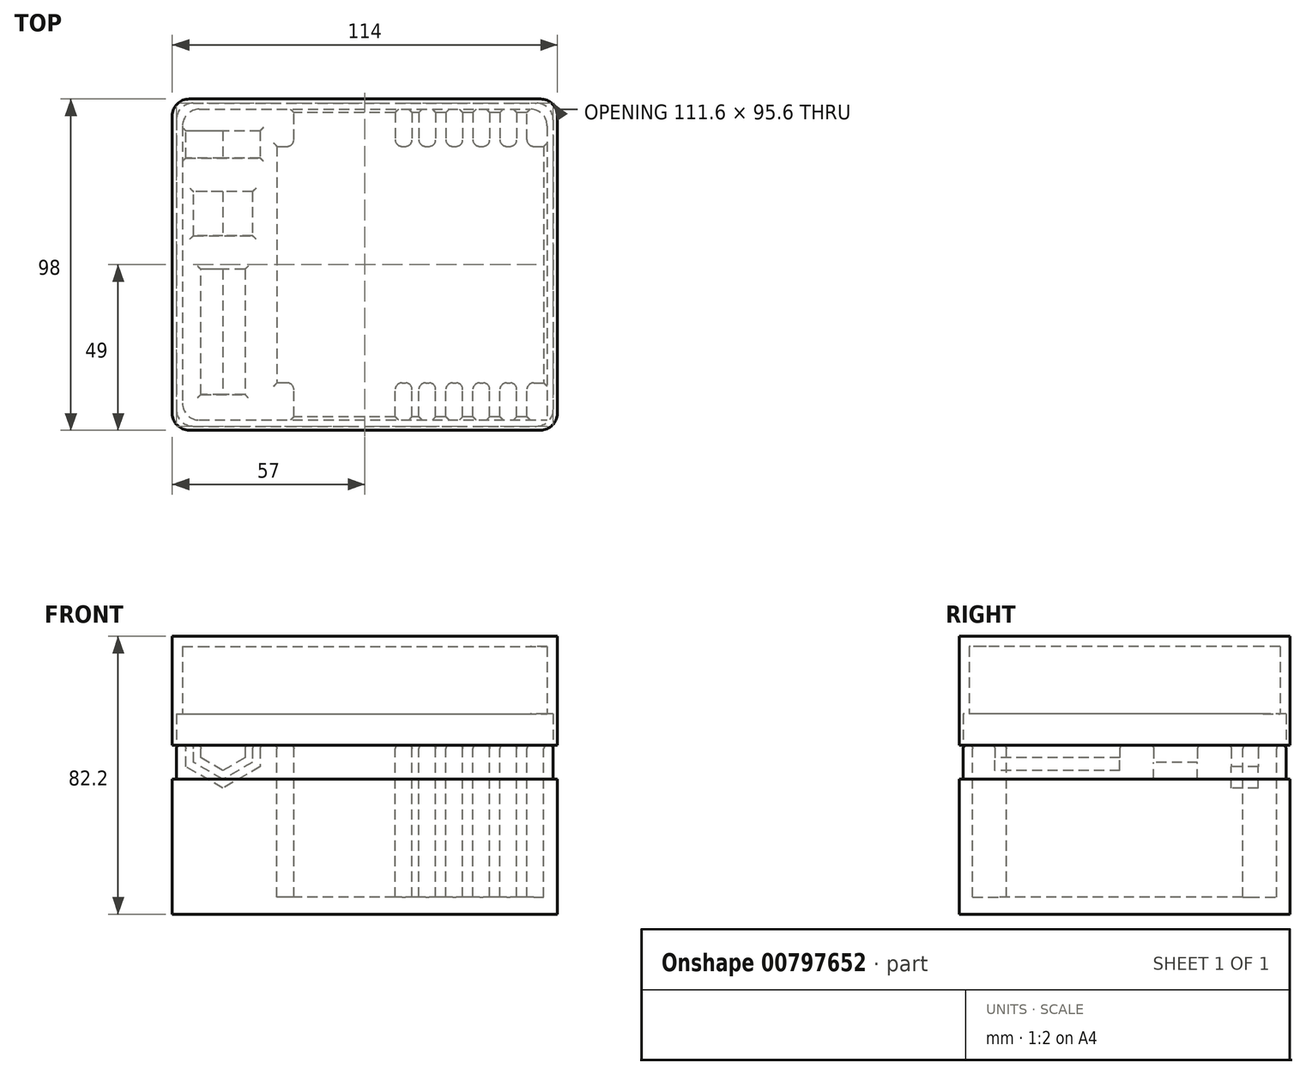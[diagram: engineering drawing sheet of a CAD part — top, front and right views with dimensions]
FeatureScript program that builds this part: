
annotation { "Feature Type Name" : "Feature", "Feature Type Description" : "" }
export const myFeature = defineFeature(function(context is Context, id is Id, definition is map)
    precondition{}
    {
        {
            var Q0;
            Q0=qCreatedBy(makeId("Top.planeOp"),FACE);
            var sketch = newSketch(context, id + "F0", { "sketchPlane" : qUnion([Q0])});
            skLineSegment(sketch, "E0.bottom", {"start": v(34.5, -45) * mm, "end": v(31.5, -45) * mm});
            skLineSegment(sketch, "E0.top", {"start": v(34.5, 45) * mm, "end": v(31.5, 45) * mm});
            skLineSegment(sketch, "E0.left", {"start": v(34.5, -45) * mm, "end": v(34.5, -35) * mm});
            skLineSegment(sketch, "E0.right", {"start": v(-34.5, -45) * mm, "end": v(-34.5, -35) * mm});
            skPoint(sketch, "E0.middle", {"position": v(0, 0) * mm});
            skLineSegment(sketch, "E1.top", {"start": v(-4.5, 35) * mm, "end": v(0.5, 35) * mm});
            skLineSegment(sketch, "E1.left", {"start": v(-4.5, 45) * mm, "end": v(-4.5, 35) * mm});
            skLineSegment(sketch, "E1.right", {"start": v(0.5, 45) * mm, "end": v(0.5, 35) * mm});
            skLineSegment(sketch, "E2.top", {"start": v(2.5, 35) * mm, "end": v(7.5, 35) * mm});
            skLineSegment(sketch, "E2.left", {"start": v(2.5, 45) * mm, "end": v(2.5, 35) * mm});
            skLineSegment(sketch, "E2.right", {"start": v(7.5, 45) * mm, "end": v(7.5, 35) * mm});
            skLineSegment(sketch, "E3.top", {"start": v(10.5, 35) * mm, "end": v(15.5, 35) * mm});
            skLineSegment(sketch, "E3.left", {"start": v(10.5, 45) * mm, "end": v(10.5, 35) * mm});
            skLineSegment(sketch, "E3.right", {"start": v(15.5, 45) * mm, "end": v(15.5, 35) * mm});
            skLineSegment(sketch, "E4.top", {"start": v(18.5, 35) * mm, "end": v(23.5, 35) * mm});
            skLineSegment(sketch, "E4.left", {"start": v(18.5, 45) * mm, "end": v(18.5, 35) * mm});
            skLineSegment(sketch, "E4.right", {"start": v(23.5, 45) * mm, "end": v(23.5, 35) * mm});
            skLineSegment(sketch, "E5.top", {"start": v(26.5, 35) * mm, "end": v(31.5, 35) * mm});
            skLineSegment(sketch, "E5.left", {"start": v(26.5, 45) * mm, "end": v(26.5, 35) * mm});
            skLineSegment(sketch, "E5.right", {"start": v(31.5, 45) * mm, "end": v(31.5, 35) * mm});
            skLineSegment(sketch, "E6.trimOffspring", {"start": v(-4.5, 45) * mm, "end": v(-34.5, 45) * mm});
            skLineSegment(sketch, "E7.trimOffspring", {"start": v(2.5, 45) * mm, "end": v(0.5, 45) * mm});
            skLineSegment(sketch, "E8.trimOffspring", {"start": v(10.5, 45) * mm, "end": v(7.5, 45) * mm});
            skLineSegment(sketch, "E9.trimOffspring", {"start": v(18.5, 45) * mm, "end": v(15.5, 45) * mm});
            skLineSegment(sketch, "E10.trimOffspring", {"start": v(26.5, 45) * mm, "end": v(23.5, 45) * mm});
            skLineSegment(sketch, "E11.MirrorCS", {"start": v(-4.5, -45) * mm, "end": v(-4.5, -35) * mm});
            skLineSegment(sketch, "E12.MirrorCS", {"start": v(0.5, -45) * mm, "end": v(0.5, -35) * mm});
            skLineSegment(sketch, "E13.MirrorCS", {"start": v(2.5, -45) * mm, "end": v(0.5, -45) * mm});
            skLineSegment(sketch, "E14.MirrorCS", {"start": v(2.5, -45) * mm, "end": v(2.5, -35) * mm});
            skLineSegment(sketch, "E15.MirrorCS", {"start": v(7.5, -45) * mm, "end": v(7.5, -35) * mm});
            skLineSegment(sketch, "E16.MirrorCS", {"start": v(10.5, -45) * mm, "end": v(7.5, -45) * mm});
            skLineSegment(sketch, "E17.MirrorCS", {"start": v(10.5, -45) * mm, "end": v(10.5, -35) * mm});
            skLineSegment(sketch, "E18.MirrorCS", {"start": v(15.5, -45) * mm, "end": v(15.5, -35) * mm});
            skLineSegment(sketch, "E19.MirrorCS", {"start": v(18.5, -45) * mm, "end": v(18.5, -35) * mm});
            skLineSegment(sketch, "E20.MirrorCS", {"start": v(18.5, -45) * mm, "end": v(15.5, -45) * mm});
            skLineSegment(sketch, "E21.MirrorCS", {"start": v(26.5, -45) * mm, "end": v(23.5, -45) * mm});
            skLineSegment(sketch, "E22.MirrorCS", {"start": v(23.5, -45) * mm, "end": v(23.5, -35) * mm});
            skLineSegment(sketch, "E23.MirrorCS", {"start": v(26.5, -45) * mm, "end": v(26.5, -35) * mm});
            skLineSegment(sketch, "E24.MirrorCS", {"start": v(31.5, -45) * mm, "end": v(31.5, -35) * mm});
            skLineSegment(sketch, "E25.MirrorCS", {"start": v(-4.5, -35) * mm, "end": v(0.5, -35) * mm});
            skLineSegment(sketch, "E26.MirrorCS", {"start": v(2.5, -35) * mm, "end": v(7.5, -35) * mm});
            skLineSegment(sketch, "E27.MirrorCS", {"start": v(10.5, -35) * mm, "end": v(15.5, -35) * mm});
            skLineSegment(sketch, "E28.MirrorCS", {"start": v(18.5, -35) * mm, "end": v(23.5, -35) * mm});
            skLineSegment(sketch, "E29.MirrorCS", {"start": v(26.5, -35) * mm, "end": v(31.5, -35) * mm});
            skLineSegment(sketch, "E30", {"start": v(-39.5, 35) * mm, "end": v(-39.5, -35) * mm});
            skLineSegment(sketch, "E31", {"start": v(-39.5, 35) * mm, "end": v(-34.5, 35) * mm});
            skLineSegment(sketch, "E32", {"start": v(-34.5, -35) * mm, "end": v(-39.5, -35) * mm});
            skLineSegment(sketch, "E33", {"start": v(39.5, 35) * mm, "end": v(39.5, -35) * mm});
            skLineSegment(sketch, "E34", {"start": v(34.5, 35) * mm, "end": v(39.5, 35) * mm});
            skLineSegment(sketch, "E35.trimOffspring", {"start": v(-34.5, 35) * mm, "end": v(-34.5, 45) * mm});
            skLineSegment(sketch, "E36.trimOffspring", {"start": v(34.5, 35) * mm, "end": v(34.5, 45) * mm});
            skLineSegment(sketch, "E37", {"start": v(34.5, -35) * mm, "end": v(39.5, -35) * mm});
            skPoint(sketch, "E38.orphan", {"position": v(-39.5, -45) * mm});
            skLineSegment(sketch, "E39.trimOffspring", {"start": v(-4.5, -45) * mm, "end": v(-34.5, -45) * mm});
            skLineSegment(sketch, "E40", {"start": v(-55.5, 78.4) * mm, "end": v(-55.5, -67.4) * mm, "construction": true});
            skLineSegment(sketch, "E41.bottom", {"start": v(-44.5, 31.59) * mm, "end": v(-66.5, 31.59) * mm});
            skLineSegment(sketch, "E41.top", {"start": v(-44.5, 39.59) * mm, "end": v(-66.5, 39.59) * mm});
            skLineSegment(sketch, "E41.left", {"start": v(-44.5, 31.59) * mm, "end": v(-44.5, 39.59) * mm});
            skLineSegment(sketch, "E41.right", {"start": v(-66.5, 31.59) * mm, "end": v(-66.5, 39.59) * mm});
            skPoint(sketch, "E41.middle", {"position": v(-55.5, 35.59) * mm});
            skLineSegment(sketch, "E42.bottom", {"start": v(-46.75, 8.59) * mm, "end": v(-64.25, 8.59) * mm});
            skLineSegment(sketch, "E42.top", {"start": v(-46.75, 21.59) * mm, "end": v(-64.25, 21.59) * mm});
            skLineSegment(sketch, "E42.left", {"start": v(-46.75, 8.59) * mm, "end": v(-46.75, 21.59) * mm});
            skLineSegment(sketch, "E42.right", {"start": v(-64.25, 8.59) * mm, "end": v(-64.25, 21.59) * mm});
            skPoint(sketch, "E42.middle", {"position": v(-55.5, 15.09) * mm});
            skLineSegment(sketch, "E43.bottom", {"start": v(-49, -38.41) * mm, "end": v(-62, -38.41) * mm});
            skLineSegment(sketch, "E43.top", {"start": v(-49, -1.41) * mm, "end": v(-62, -1.41) * mm});
            skLineSegment(sketch, "E43.left", {"start": v(-49, -38.41) * mm, "end": v(-49, -1.41) * mm});
            skLineSegment(sketch, "E43.right", {"start": v(-62, -38.41) * mm, "end": v(-62, -1.41) * mm});
            skPoint(sketch, "E43.middle", {"position": v(-55.5, -19.91) * mm});
            skLineSegment(sketch, "E44.bottom", {"start": v(-70.5, 49) * mm, "end": v(43.5, 49) * mm});
            skLineSegment(sketch, "E44.top", {"start": v(-70.5, -49) * mm, "end": v(43.5, -49) * mm});
            skLineSegment(sketch, "E44.left", {"start": v(-70.5, 49) * mm, "end": v(-70.5, -49) * mm});
            skLineSegment(sketch, "E44.right", {"start": v(43.5, 49) * mm, "end": v(43.5, -49) * mm});
            skSolve(sketch);
        }
        {
            var Q0;
            Q0=makeQuery(id+"F0.imprint","IMPRINT",FACE,{"disambiguationData":[TD([[makeQuery(id+"F0.imprint","IMPRINT",EDGE,{"derivedFrom":sQuery(id+"F0.wireOp",EDGE,"E0.top")}),-1.0]])]});
            var Q1;
            Q1=makeQuery(id+"F0.imprint","IMPRINT",FACE,{"disambiguationData":[TD([[makeQuery(id+"F0.imprint","IMPRINT",EDGE,{"derivedFrom":sQuery(id+"F0.wireOp",EDGE,"E41.bottom")}),-1.0]])]});
            var Q2;
            Q2=makeQuery(id+"F0.imprint","IMPRINT",FACE,{"disambiguationData":[TD([[makeQuery(id+"F0.imprint","IMPRINT",EDGE,{"derivedFrom":sQuery(id+"F0.wireOp",EDGE,"E42.bottom")}),-1.0]])]});
            var Q3;
            Q3=makeQuery(id+"F0.imprint","IMPRINT",FACE,{"disambiguationData":[TD([[makeQuery(id+"F0.imprint","IMPRINT",EDGE,{"derivedFrom":sQuery(id+"F0.wireOp",EDGE,"E43.bottom")}),-1.0]])]});
            extrude(context, id + "F1", {"entities" : qUnion([Q0, Q1, Q2, Q3]), "oppositeDirection" : true, "depth" : 45 * mm, "offsetDistance" : 25 * mm});
        }
        {
            var Q0;
            Q0=makeQuery(id+"F1.opExtrude","SWEPT_FACE",FACE,{"disambiguationData":[OSD([sQuery(id+"F0.wireOp",EDGE,"E44.top")])]});
            var sketch = newSketch(context, id + "F2", { "sketchPlane" : qUnion([Q0])});
            skLineSegment(sketch, "E45.bottom", {"start": v(-70.5, -45) * mm, "end": v(43.5, -45) * mm});
            skLineSegment(sketch, "E45.top", {"start": v(-70.5, -50) * mm, "end": v(43.5, -50) * mm});
            skLineSegment(sketch, "E45.left", {"start": v(-70.5, -45) * mm, "end": v(-70.5, -50) * mm});
            skLineSegment(sketch, "E45.right", {"start": v(43.5, -45) * mm, "end": v(43.5, -50) * mm});
            skSolve(sketch);
        }
        {
            var Q0;
            Q0=makeQuery(id+"F2.imprint","IMPRINT",FACE,{"disambiguationData":[TD([[makeQuery(id+"F2.imprint","IMPRINT",EDGE,{"derivedFrom":sQuery(id+"F2.wireOp",EDGE,"E45.bottom")}),-1.0]])]});
            var Q1;
            Q1=makeQuery(id+"F1.opExtrude","SWEPT_FACE",FACE,{"disambiguationData":[OSD([sQuery(id+"F0.wireOp",EDGE,"E44.bottom")])]});
            extrude(context, id + "F3", {"entities" : qUnion([Q0]), "operationType" : NewBodyOperationType.ADD, "endBound" : BoundingType.UP_TO_SURFACE, "oppositeDirection" : true, "depth" : 25 * mm, "endBoundEntityFace" : qUnion([Q1]), "offsetDistance" : 25 * mm});
        }
        {
            var Q0;
            Q0=makeQuery(id+"F1.opExtrude","SWEPT_EDGE",EDGE,{"disambiguationData":[OSD([sQuery(id+"F0.wireOp",EDGE,"E31"),sQuery(id+"F0.wireOp",EDGE,"E35.trimOffspring")])]});
            var Q1;
            Q1=makeQuery(id+"F1.opExtrude","SWEPT_EDGE",EDGE,{"disambiguationData":[OSD([sQuery(id+"F0.wireOp",EDGE,"E1.top"),sQuery(id+"F0.wireOp",EDGE,"E1.left")])]});
            var Q2;
            Q2=makeQuery(id+"F1.opExtrude","SWEPT_EDGE",EDGE,{"disambiguationData":[OSD([sQuery(id+"F0.wireOp",EDGE,"E1.top"),sQuery(id+"F0.wireOp",EDGE,"E1.right")])]});
            var Q3;
            Q3=makeQuery(id+"F1.opExtrude","SWEPT_EDGE",EDGE,{"disambiguationData":[OSD([sQuery(id+"F0.wireOp",EDGE,"E2.top"),sQuery(id+"F0.wireOp",EDGE,"E2.left")])]});
            var Q4;
            Q4=makeQuery(id+"F1.opExtrude","SWEPT_EDGE",EDGE,{"disambiguationData":[OSD([sQuery(id+"F0.wireOp",EDGE,"E2.top"),sQuery(id+"F0.wireOp",EDGE,"E2.right")])]});
            var Q5;
            Q5=makeQuery(id+"F1.opExtrude","SWEPT_EDGE",EDGE,{"disambiguationData":[OSD([sQuery(id+"F0.wireOp",EDGE,"E3.top"),sQuery(id+"F0.wireOp",EDGE,"E3.left")])]});
            var Q6;
            Q6=makeQuery(id+"F1.opExtrude","SWEPT_EDGE",EDGE,{"disambiguationData":[OSD([sQuery(id+"F0.wireOp",EDGE,"E3.top"),sQuery(id+"F0.wireOp",EDGE,"E3.right")])]});
            var Q7;
            Q7=makeQuery(id+"F1.opExtrude","SWEPT_EDGE",EDGE,{"disambiguationData":[OSD([sQuery(id+"F0.wireOp",EDGE,"E4.top"),sQuery(id+"F0.wireOp",EDGE,"E4.left")])]});
            var Q8;
            Q8=makeQuery(id+"F1.opExtrude","SWEPT_EDGE",EDGE,{"disambiguationData":[OSD([sQuery(id+"F0.wireOp",EDGE,"E4.top"),sQuery(id+"F0.wireOp",EDGE,"E4.right")])]});
            var Q9;
            Q9=makeQuery(id+"F1.opExtrude","SWEPT_EDGE",EDGE,{"disambiguationData":[OSD([sQuery(id+"F0.wireOp",EDGE,"E5.top"),sQuery(id+"F0.wireOp",EDGE,"E5.left")])]});
            var Q10;
            Q10=makeQuery(id+"F1.opExtrude","SWEPT_EDGE",EDGE,{"disambiguationData":[OSD([sQuery(id+"F0.wireOp",EDGE,"E5.top"),sQuery(id+"F0.wireOp",EDGE,"E5.right")])]});
            var Q11;
            Q11=makeQuery(id+"F1.opExtrude","SWEPT_EDGE",EDGE,{"disambiguationData":[OSD([sQuery(id+"F0.wireOp",EDGE,"E34"),sQuery(id+"F0.wireOp",EDGE,"E36.trimOffspring")])]});
            var Q12;
            Q12=makeQuery(id+"F1.opExtrude","SWEPT_EDGE",EDGE,{"disambiguationData":[OSD([sQuery(id+"F0.wireOp",EDGE,"E0.right"),sQuery(id+"F0.wireOp",EDGE,"E32")])]});
            var Q13;
            Q13=makeQuery(id+"F1.opExtrude","SWEPT_EDGE",EDGE,{"disambiguationData":[OSD([sQuery(id+"F0.wireOp",EDGE,"E11.MirrorCS"),sQuery(id+"F0.wireOp",EDGE,"E25.MirrorCS")])]});
            var Q14;
            Q14=makeQuery(id+"F1.opExtrude","SWEPT_EDGE",EDGE,{"disambiguationData":[OSD([sQuery(id+"F0.wireOp",EDGE,"E12.MirrorCS"),sQuery(id+"F0.wireOp",EDGE,"E25.MirrorCS")])]});
            var Q15;
            Q15=makeQuery(id+"F1.opExtrude","SWEPT_EDGE",EDGE,{"disambiguationData":[OSD([sQuery(id+"F0.wireOp",EDGE,"E14.MirrorCS"),sQuery(id+"F0.wireOp",EDGE,"E26.MirrorCS")])]});
            var Q16;
            Q16=makeQuery(id+"F1.opExtrude","SWEPT_EDGE",EDGE,{"disambiguationData":[OSD([sQuery(id+"F0.wireOp",EDGE,"E15.MirrorCS"),sQuery(id+"F0.wireOp",EDGE,"E26.MirrorCS")])]});
            var Q17;
            Q17=makeQuery(id+"F1.opExtrude","SWEPT_EDGE",EDGE,{"disambiguationData":[OSD([sQuery(id+"F0.wireOp",EDGE,"E17.MirrorCS"),sQuery(id+"F0.wireOp",EDGE,"E27.MirrorCS")])]});
            var Q18;
            Q18=makeQuery(id+"F1.opExtrude","SWEPT_EDGE",EDGE,{"disambiguationData":[OSD([sQuery(id+"F0.wireOp",EDGE,"E18.MirrorCS"),sQuery(id+"F0.wireOp",EDGE,"E27.MirrorCS")])]});
            var Q19;
            Q19=makeQuery(id+"F1.opExtrude","SWEPT_EDGE",EDGE,{"disambiguationData":[OSD([sQuery(id+"F0.wireOp",EDGE,"E19.MirrorCS"),sQuery(id+"F0.wireOp",EDGE,"E28.MirrorCS")])]});
            var Q20;
            Q20=makeQuery(id+"F1.opExtrude","SWEPT_EDGE",EDGE,{"disambiguationData":[OSD([sQuery(id+"F0.wireOp",EDGE,"E22.MirrorCS"),sQuery(id+"F0.wireOp",EDGE,"E28.MirrorCS")])]});
            var Q21;
            Q21=makeQuery(id+"F1.opExtrude","SWEPT_EDGE",EDGE,{"disambiguationData":[OSD([sQuery(id+"F0.wireOp",EDGE,"E23.MirrorCS"),sQuery(id+"F0.wireOp",EDGE,"E29.MirrorCS")])]});
            var Q22;
            Q22=makeQuery(id+"F1.opExtrude","SWEPT_EDGE",EDGE,{"disambiguationData":[OSD([sQuery(id+"F0.wireOp",EDGE,"E24.MirrorCS"),sQuery(id+"F0.wireOp",EDGE,"E29.MirrorCS")])]});
            var Q23;
            Q23=makeQuery(id+"F1.opExtrude","SWEPT_EDGE",EDGE,{"disambiguationData":[OSD([sQuery(id+"F0.wireOp",EDGE,"E0.left"),sQuery(id+"F0.wireOp",EDGE,"E37")])]});
            fillet(context, id + "F4", {"entities" : qUnion([Q0, Q1, Q2, Q3, Q4, Q5, Q6, Q7, Q8, Q9, Q10, Q11, Q12, Q13, Q14, Q15, Q16, Q17, Q18, Q19, Q20, Q21, Q22, Q23]), "radius" : 2 * mm, "tangentPropagation" : true, "allowEdgeOverflow" : false});
        }
        {
            var Q0;
            Q0=qCreatedBy(makeId("Front.planeOp"),FACE);
            var Q1;
            Q1=sQuery(id+"F0.wireOp",VERTEX,"E41.bottom.start");
            cPlane(context, id + "F5", {"entities" : qUnion([Q0, Q1]), "cplaneType" : CPlaneType.PLANE_POINT, "offset" : 25 * mm, "oppositeDirection" : true, "width" : 150 * mm, "height" : 150 * mm});
        }
        {
            var Q0;
            Q0=qCreatedBy(makeId("Front.planeOp"),FACE);
            var Q1;
            Q1=sQuery(id+"F0.wireOp",VERTEX,"E42.bottom.start");
            cPlane(context, id + "F6", {"entities" : qUnion([Q0, Q1]), "cplaneType" : CPlaneType.PLANE_POINT, "offset" : 25 * mm, "width" : 150 * mm, "height" : 150 * mm});
        }
        {
            var Q0;
            Q0=qCreatedBy(makeId("Front.planeOp"),FACE);
            var Q1;
            Q1=sQuery(id+"F0.wireOp",VERTEX,"E43.bottom.start");
            cPlane(context, id + "F7", {"entities" : qUnion([Q0, Q1]), "cplaneType" : CPlaneType.PLANE_POINT, "offset" : 25 * mm, "width" : 150 * mm, "height" : 150 * mm});
        }
        {
            var Q0;
            Q0=sQuery(id+"F0.wireOp",EDGE,"E40");
            cPoint(context, id + "F8", {"entities" : qUnion([Q0]), "parameter" : 0.5});
        }
        {
            var Q0;
            Q0=qCreatedBy(makeId("Right.planeOp"),FACE);
            var Q1;
            Q1 = qCreatedBy(id + "F8" ,VERTEX);
            cPlane(context, id + "F9", {"entities" : qUnion([Q0, Q1]), "cplaneType" : CPlaneType.PLANE_POINT, "offset" : 25 * mm, "width" : 150 * mm, "height" : 150 * mm});
        }
        {
            var Q0;
            Q0=sQuery(id+"F0.wireOp",VERTEX,"E41.top.end");
            var Q1;
            Q1=qCreatedBy(id+"F9.planeOp",FACE);
            cPlane(context, id + "F10", {"entities" : qUnion([Q0, Q1]), "cplaneType" : CPlaneType.PLANE_POINT, "offset" : 25 * mm, "width" : 150 * mm, "height" : 150 * mm});
        }
        {
            var Q0;
            Q0=qCreatedBy(id+"F9.planeOp",FACE);
            var Q1;
            Q1=sQuery(id+"F0.wireOp",VERTEX,"E41.top.start");
            cPlane(context, id + "F11", {"entities" : qUnion([Q0, Q1]), "cplaneType" : CPlaneType.PLANE_POINT, "offset" : 25 * mm, "width" : 150 * mm, "height" : 150 * mm});
        }
        {
            var Q0;
            Q0=qCreatedBy(id+"F5.planeOp",FACE);
            var sketch = newSketch(context, id + "F12", { "sketchPlane" : qUnion([Q0])});
            skPoint(sketch, "E46", {"position": v(-55.5, 0) * mm});
            skPoint(sketch, "E47", {"position": v(-66.5, 0) * mm});
            skPoint(sketch, "E48", {"position": v(-44.5, 0) * mm});
            skCircle(sketch, "E49.cCircle", {"center": v(-55.5, 0) * mm, "radius": 11 * mm, "construction": true});
            skLineSegment(sketch, "E49.0", {"start": v(-44.5, 6.35) * mm, "end": v(-44.5, -6.35) * mm});
            skLineSegment(sketch, "E49.1", {"start": v(-44.5, -6.35) * mm, "end": v(-55.5, -12.7) * mm});
            skLineSegment(sketch, "E49.2", {"start": v(-55.5, -12.7) * mm, "end": v(-66.5, -6.35) * mm});
            skLineSegment(sketch, "E49.3", {"start": v(-66.5, -6.35) * mm, "end": v(-66.5, 6.35) * mm});
            skLineSegment(sketch, "E49.4", {"start": v(-66.5, 6.35) * mm, "end": v(-55.5, 12.7) * mm});
            skLineSegment(sketch, "E49.5", {"start": v(-55.5, 12.7) * mm, "end": v(-44.5, 6.35) * mm});
            skSolve(sketch);
        }
        {
            var Q0;
            Q0=qCreatedBy(id+"F9.planeOp",FACE);
            var Q1;
            Q1=sQuery(id+"F0.wireOp",VERTEX,"E42.bottom.end");
            cPlane(context, id + "F13", {"entities" : qUnion([Q0, Q1]), "cplaneType" : CPlaneType.PLANE_POINT, "offset" : 25 * mm, "width" : 150 * mm, "height" : 150 * mm});
        }
        {
            var Q0;
            Q0=qCreatedBy(id+"F9.planeOp",FACE);
            var Q1;
            Q1=sQuery(id+"F0.wireOp",VERTEX,"E42.bottom.start");
            cPlane(context, id + "F14", {"entities" : qUnion([Q0, Q1]), "cplaneType" : CPlaneType.PLANE_POINT, "offset" : 25 * mm, "width" : 150 * mm, "height" : 150 * mm});
        }
        {
            var Q0;
            Q0=qCreatedBy(id+"F6.planeOp",FACE);
            var sketch = newSketch(context, id + "F15", { "sketchPlane" : qUnion([Q0])});
            skPoint(sketch, "E50", {"position": v(-64.25, 0) * mm});
            skPoint(sketch, "E51", {"position": v(-55.5, 0) * mm});
            skPoint(sketch, "E52", {"position": v(-46.75, 0) * mm});
            skCircle(sketch, "E53.cCircle", {"center": v(-55.5, 0) * mm, "radius": 8.75 * mm, "construction": true});
            skLineSegment(sketch, "E53.0", {"start": v(-46.75, 5.05) * mm, "end": v(-46.75, -5.05) * mm});
            skLineSegment(sketch, "E53.1", {"start": v(-46.75, -5.05) * mm, "end": v(-55.5, -10.1) * mm});
            skLineSegment(sketch, "E53.2", {"start": v(-55.5, -10.1) * mm, "end": v(-64.25, -5.05) * mm});
            skLineSegment(sketch, "E53.3", {"start": v(-64.25, -5.05) * mm, "end": v(-64.25, 5.05) * mm});
            skLineSegment(sketch, "E53.4", {"start": v(-64.25, 5.05) * mm, "end": v(-55.5, 10.1) * mm});
            skLineSegment(sketch, "E53.5", {"start": v(-55.5, 10.1) * mm, "end": v(-46.75, 5.05) * mm});
            skSolve(sketch);
        }
        {
            var Q0;
            Q0=qCreatedBy(id+"F9.planeOp",FACE);
            var Q1;
            Q1=sQuery(id+"F0.wireOp",VERTEX,"E43.bottom.end");
            cPlane(context, id + "F16", {"entities" : qUnion([Q0, Q1]), "cplaneType" : CPlaneType.PLANE_POINT, "offset" : 25 * mm, "width" : 150 * mm, "height" : 150 * mm});
        }
        {
            var Q0;
            Q0=qCreatedBy(id+"F16.planeOp",FACE);
            var Q1;
            Q1=sQuery(id+"F0.wireOp",VERTEX,"E43.bottom.start");
            cPlane(context, id + "F17", {"entities" : qUnion([Q0, Q1]), "cplaneType" : CPlaneType.PLANE_POINT, "offset" : 25 * mm, "width" : 150 * mm, "height" : 150 * mm});
        }
        {
            var Q0;
            Q0=qCreatedBy(id+"F7.planeOp",FACE);
            var sketch = newSketch(context, id + "F18", { "sketchPlane" : qUnion([Q0])});
            skPoint(sketch, "E54", {"position": v(-62, 0) * mm});
            skPoint(sketch, "E55", {"position": v(-55.5, 0) * mm});
            skPoint(sketch, "E56", {"position": v(-49, 0) * mm});
            skCircle(sketch, "E57.cCircle", {"center": v(-55.5, 0) * mm, "radius": 6.5 * mm, "construction": true});
            skLineSegment(sketch, "E57.0", {"start": v(-49, 3.75) * mm, "end": v(-49, -3.75) * mm});
            skLineSegment(sketch, "E57.1", {"start": v(-49, -3.75) * mm, "end": v(-55.5, -7.5) * mm});
            skLineSegment(sketch, "E57.2", {"start": v(-55.5, -7.5) * mm, "end": v(-62, -3.75) * mm});
            skLineSegment(sketch, "E57.3", {"start": v(-62, -3.75) * mm, "end": v(-62, 3.75) * mm});
            skLineSegment(sketch, "E57.4", {"start": v(-62, 3.75) * mm, "end": v(-55.5, 7.5) * mm});
            skLineSegment(sketch, "E57.5", {"start": v(-55.5, 7.5) * mm, "end": v(-49, 3.75) * mm});
            skSolve(sketch);
        }
        {
            var Q0;
            Q0=makeQuery(id+"F12.imprint","IMPRINT",FACE,{"disambiguationData":[TD([[makeQuery(id+"F12.imprint","IMPRINT",EDGE,{"derivedFrom":sQuery(id+"F12.wireOp",EDGE,"E49.0")}),-1.0]])]});
            var Q1;
            Q1=sQuery(id+"F0.wireOp",VERTEX,"E41.top.end");
            extrude(context, id + "F19", {"entities" : qUnion([Q0]), "operationType" : NewBodyOperationType.REMOVE, "endBound" : BoundingType.UP_TO_VERTEX, "oppositeDirection" : true, "depth" : 25 * mm, "endBoundEntityVertex" : qUnion([Q1]), "offsetDistance" : 25 * mm});
        }
        {
            var Q0;
            Q0=makeQuery(id+"F15.imprint","IMPRINT",FACE,{"disambiguationData":[TD([[makeQuery(id+"F15.imprint","IMPRINT",EDGE,{"derivedFrom":sQuery(id+"F15.wireOp",EDGE,"E53.0")}),-1.0]])]});
            var Q1;
            Q1=sQuery(id+"F0.wireOp",VERTEX,"E42.top.end");
            extrude(context, id + "F20", {"entities" : qUnion([Q0]), "operationType" : NewBodyOperationType.REMOVE, "endBound" : BoundingType.UP_TO_VERTEX, "oppositeDirection" : true, "depth" : 25 * mm, "endBoundEntityVertex" : qUnion([Q1]), "offsetDistance" : 25 * mm});
        }
        {
            var Q0;
            Q0=makeQuery(id+"F18.imprint","IMPRINT",FACE,{"disambiguationData":[TD([[makeQuery(id+"F18.imprint","IMPRINT",EDGE,{"derivedFrom":sQuery(id+"F18.wireOp",EDGE,"E57.0")}),-1.0]])]});
            var Q1;
            Q1=sQuery(id+"F0.wireOp",VERTEX,"E43.top.end");
            extrude(context, id + "F21", {"entities" : qUnion([Q0]), "operationType" : NewBodyOperationType.REMOVE, "endBound" : BoundingType.UP_TO_VERTEX, "oppositeDirection" : true, "depth" : 25 * mm, "endBoundEntityVertex" : qUnion([Q1]), "offsetDistance" : 25 * mm});
        }
        {
            var Q0;
            Q0=makeQuery(id+"F0.imprint","IMPRINT",FACE,{"disambiguationData":[TD([[makeQuery(id+"F0.imprint","IMPRINT",EDGE,{"derivedFrom":sQuery(id+"F0.wireOp",EDGE,"E0.top")}),-1.0]])]});
            var sketch = newSketch(context, id + "F22", { "sketchPlane" : qUnion([Q0])});
            skLineSegment(sketch, "E58.0", {"start": v(-69.3, 47.8) * mm, "end": v(-69.3, -47.8) * mm});
            skLineSegment(sketch, "E58.1", {"start": v(-69.3, 47.8) * mm, "end": v(42.3, 47.8) * mm});
            skLineSegment(sketch, "E58.2", {"start": v(42.3, 47.8) * mm, "end": v(42.3, -47.8) * mm});
            skLineSegment(sketch, "E58.3", {"start": v(-69.3, -47.8) * mm, "end": v(42.3, -47.8) * mm});
            skSolve(sketch);
        }
        {
            var Q0;
            Q0=makeQuery(id+"F22.imprint","IMPRINT",FACE,{"disambiguationData":[TD([[makeQuery(id+"F22.imprint","IMPRINT",EDGE,{"derivedFrom":sQuery(id+"F22.wireOp",EDGE,"E58.0")}),-1.0]])]});
            var Q1;
            Q1=sQuery(id+"F0.wireOp",EDGE,"E44.top");
            var Q2;
            Q2=sQuery(id+"F22.wireOp",EDGE,"E58.3");
            extrude(context, id + "F23", {"entities" : qUnion([Q0]), "operationType" : NewBodyOperationType.REMOVE, "surfaceEntities" : qUnion([Q1, Q2]), "oppositeDirection" : true, "depth" : 10 * mm, "offsetDistance" : 25 * mm});
        }
        {
            var Q0;
            Q0=makeQuery(id+"F1.opExtrude","CAP_FACE",FACE,{"disambiguationData":[OSD([sQuery(id+"F0.wireOp",EDGE,"E0.top"),sQuery(id+"F0.wireOp",EDGE,"E0.left"),sQuery(id+"F0.wireOp",EDGE,"E0.right"),sQuery(id+"F0.wireOp",EDGE,"E1.top"),sQuery(id+"F0.wireOp",EDGE,"E1.left"),sQuery(id+"F0.wireOp",EDGE,"E1.right"),sQuery(id+"F0.wireOp",EDGE,"E2.top"),sQuery(id+"F0.wireOp",EDGE,"E2.left"),sQuery(id+"F0.wireOp",EDGE,"E2.right"),sQuery(id+"F0.wireOp",EDGE,"E3.top"),sQuery(id+"F0.wireOp",EDGE,"E3.left"),sQuery(id+"F0.wireOp",EDGE,"E3.right"),sQuery(id+"F0.wireOp",EDGE,"E4.top"),sQuery(id+"F0.wireOp",EDGE,"E4.left"),sQuery(id+"F0.wireOp",EDGE,"E4.right"),sQuery(id+"F0.wireOp",EDGE,"E5.top"),sQuery(id+"F0.wireOp",EDGE,"E5.left"),sQuery(id+"F0.wireOp",EDGE,"E5.right"),sQuery(id+"F0.wireOp",EDGE,"E6.trimOffspring"),sQuery(id+"F0.wireOp",EDGE,"E7.trimOffspring"),sQuery(id+"F0.wireOp",EDGE,"E8.trimOffspring"),sQuery(id+"F0.wireOp",EDGE,"E9.trimOffspring"),sQuery(id+"F0.wireOp",EDGE,"E10.trimOffspring"),sQuery(id+"F0.wireOp",EDGE,"E11.MirrorCS"),sQuery(id+"F0.wireOp",EDGE,"E12.MirrorCS"),sQuery(id+"F0.wireOp",EDGE,"E14.MirrorCS"),sQuery(id+"F0.wireOp",EDGE,"E15.MirrorCS"),sQuery(id+"F0.wireOp",EDGE,"E17.MirrorCS"),sQuery(id+"F0.wireOp",EDGE,"E18.MirrorCS"),sQuery(id+"F0.wireOp",EDGE,"E19.MirrorCS"),sQuery(id+"F0.wireOp",EDGE,"E22.MirrorCS"),sQuery(id+"F0.wireOp",EDGE,"E23.MirrorCS"),sQuery(id+"F0.wireOp",EDGE,"E24.MirrorCS"),sQuery(id+"F0.wireOp",EDGE,"E0.bottom"),sQuery(id+"F0.wireOp",EDGE,"E25.MirrorCS"),sQuery(id+"F0.wireOp",EDGE,"E26.MirrorCS"),sQuery(id+"F0.wireOp",EDGE,"E27.MirrorCS"),sQuery(id+"F0.wireOp",EDGE,"E28.MirrorCS"),sQuery(id+"F0.wireOp",EDGE,"E29.MirrorCS"),sQuery(id+"F0.wireOp",EDGE,"E30"),sQuery(id+"F0.wireOp",EDGE,"E31"),sQuery(id+"F0.wireOp",EDGE,"E32"),sQuery(id+"F0.wireOp",EDGE,"E33"),sQuery(id+"F0.wireOp",EDGE,"E34"),sQuery(id+"F0.wireOp",EDGE,"E35.trimOffspring"),sQuery(id+"F0.wireOp",EDGE,"E36.trimOffspring"),sQuery(id+"F0.wireOp",EDGE,"E37"),sQuery(id+"F0.wireOp",EDGE,"E39.trimOffspring"),sQuery(id+"F0.wireOp",EDGE,"E13.MirrorCS"),sQuery(id+"F0.wireOp",EDGE,"E16.MirrorCS"),sQuery(id+"F0.wireOp",EDGE,"E20.MirrorCS"),sQuery(id+"F0.wireOp",EDGE,"E21.MirrorCS"),sQuery(id+"F0.wireOp",EDGE,"E44.bottom"),sQuery(id+"F0.wireOp",EDGE,"E44.top"),sQuery(id+"F0.wireOp",EDGE,"E44.left"),sQuery(id+"F0.wireOp",EDGE,"E44.right")])],"isStart":true});
            fillet(context, id + "F24", {"entities" : qUnion([Q0]), "radius" : 1 * mm, "tangentPropagation" : true, "allowEdgeOverflow" : false});
        }
        {
            var Q0;
            Q0=makeQuery(id+"F3.boolean.opBoolean","MERGE",EDGE,{"derivedFrom":[makeQuery(id+"F1.opExtrude","SWEPT_EDGE",EDGE,{"disambiguationData":[OSD([sQuery(id+"F0.wireOp",EDGE,"E44.top"),sQuery(id+"F0.wireOp",EDGE,"E44.left")])]}),makeQuery(id+"F3.opExtrude","CAP_EDGE",EDGE,{"disambiguationData":[OSD([sQuery(id+"F2.wireOp",EDGE,"E45.left")])],"isStart":true})]});
            var Q1;
            Q1=makeQuery(id+"F23.boolean.opBoolean","COPY",EDGE,{"derivedFrom":makeQuery(id+"F23.opExtrude","SWEPT_EDGE",EDGE,{"disambiguationData":[OSD([sQuery(id+"F22.wireOp",EDGE,"E58.0"),sQuery(id+"F22.wireOp",EDGE,"E58.3")])]})});
            var Q2;
            Q2=makeQuery(id+"F23.boolean.opBoolean","COPY",EDGE,{"derivedFrom":makeQuery(id+"F23.opExtrude","SWEPT_EDGE",EDGE,{"disambiguationData":[OSD([sQuery(id+"F22.wireOp",EDGE,"E58.0"),sQuery(id+"F22.wireOp",EDGE,"E58.1")])]})});
            var Q3;
            {var subQ0=sQuery(id+"F0.wireOp",EDGE,"E44.bottom");Q3=makeQuery(id+"F3.boolean.opBoolean","MERGE",EDGE,{"derivedFrom":[makeQuery(id+"F1.opExtrude","SWEPT_EDGE",EDGE,{"disambiguationData":[OSD([subQ0,sQuery(id+"F0.wireOp",EDGE,"E44.left")])]}),makeQuery(id+"F3.opExtrude","TWEAK_EDGE",EDGE,{"derivedFrom":[makeQuery(id+"F1.opExtrude","SWEPT_FACE",FACE,{"disambiguationData":[OSD([subQ0])]}),makeQuery(id+"F2.imprint","IMPRINT",EDGE,{"derivedFrom":sQuery(id+"F2.wireOp",EDGE,"E45.left")})]})]});}
            var Q4;
            Q4=makeQuery(id+"F3.boolean.opBoolean","MERGE",EDGE,{"derivedFrom":[makeQuery(id+"F1.opExtrude","SWEPT_EDGE",EDGE,{"disambiguationData":[OSD([sQuery(id+"F0.wireOp",EDGE,"E44.top"),sQuery(id+"F0.wireOp",EDGE,"E44.right")])]}),makeQuery(id+"F3.opExtrude","CAP_EDGE",EDGE,{"disambiguationData":[OSD([sQuery(id+"F2.wireOp",EDGE,"E45.right")])],"isStart":true})]});
            var Q5;
            Q5=makeQuery(id+"F23.boolean.opBoolean","COPY",EDGE,{"derivedFrom":makeQuery(id+"F23.opExtrude","SWEPT_EDGE",EDGE,{"disambiguationData":[OSD([sQuery(id+"F22.wireOp",EDGE,"E58.2"),sQuery(id+"F22.wireOp",EDGE,"E58.3")])]})});
            var Q6;
            {var subQ0=sQuery(id+"F0.wireOp",EDGE,"E44.bottom");Q6=makeQuery(id+"F3.boolean.opBoolean","MERGE",EDGE,{"derivedFrom":[makeQuery(id+"F1.opExtrude","SWEPT_EDGE",EDGE,{"disambiguationData":[OSD([subQ0,sQuery(id+"F0.wireOp",EDGE,"E44.right")])]}),makeQuery(id+"F3.opExtrude","TWEAK_EDGE",EDGE,{"derivedFrom":[makeQuery(id+"F1.opExtrude","SWEPT_FACE",FACE,{"disambiguationData":[OSD([subQ0])]}),makeQuery(id+"F2.imprint","IMPRINT",EDGE,{"derivedFrom":sQuery(id+"F2.wireOp",EDGE,"E45.right")})]})]});}
            var Q7;
            Q7=makeQuery(id+"F23.boolean.opBoolean","COPY",EDGE,{"derivedFrom":makeQuery(id+"F23.opExtrude","SWEPT_EDGE",EDGE,{"disambiguationData":[OSD([sQuery(id+"F22.wireOp",EDGE,"E58.1"),sQuery(id+"F22.wireOp",EDGE,"E58.2")])]})});
            fillet(context, id + "F25", {"entities" : qUnion([Q0, Q1, Q2, Q3, Q4, Q5, Q6, Q7]), "radius" : 5 * mm, "tangentPropagation" : true, "allowEdgeOverflow" : false});
        }
        {
            var Q0;
            Q0=makeQuery(id+"F22.imprint","IMPRINT",FACE,{"disambiguationData":[TD([[makeQuery(id+"F22.imprint","IMPRINT",EDGE,{"derivedFrom":sQuery(id+"F22.wireOp",EDGE,"E58.0")}),-1.0]])]});
            var Q1;
            Q1=sQuery(id+"F0.wireOp",EDGE,"E44.bottom");
            var Q2;
            Q2=sQuery(id+"F22.wireOp",EDGE,"E58.1");
            extrude(context, id + "F26", {"entities" : qUnion([Q0]), "surfaceEntities" : qUnion([Q1, Q2]), "depth" : 9.2 * mm, "offsetDistance" : 25 * mm});
        }
        {
            var Q0;
            Q0=makeQuery(id+"F26.opExtrude","CAP_FACE",FACE,{"disambiguationData":[OSD([sQuery(id+"F0.wireOp",EDGE,"E44.bottom"),sQuery(id+"F0.wireOp",EDGE,"E44.top"),sQuery(id+"F0.wireOp",EDGE,"E44.left"),sQuery(id+"F0.wireOp",EDGE,"E44.right"),sQuery(id+"F22.wireOp",EDGE,"E58.0"),sQuery(id+"F22.wireOp",EDGE,"E58.1"),sQuery(id+"F22.wireOp",EDGE,"E58.2"),sQuery(id+"F22.wireOp",EDGE,"E58.3")])],"isStart":false});
            var sketch = newSketch(context, id + "F27", { "sketchPlane" : qUnion([Q0])});
            skLineSegment(sketch, "E59.0", {"start": v(-67.5, -46) * mm, "end": v(40.5, -46) * mm});
            skLineSegment(sketch, "E59.1", {"start": v(-67.5, 46) * mm, "end": v(-67.5, -46) * mm});
            skLineSegment(sketch, "E59.2", {"start": v(-67.5, 46) * mm, "end": v(40.5, 46) * mm});
            skLineSegment(sketch, "E59.3", {"start": v(40.5, 46) * mm, "end": v(40.5, -46) * mm});
            skSolve(sketch);
        }
        {
            var Q0;
            Q0=makeQuery(id+"F27.imprint","IMPRINT",FACE,{"disambiguationData":[TD([[makeQuery(id+"F27.imprint","IMPRINT",EDGE,{"derivedFrom":makeQuery(id+"F26.opExtrude","CAP_EDGE",EDGE,{"disambiguationData":[OSD([sQuery(id+"F22.wireOp",EDGE,"E58.0")])],"isStart":false})}),-1.0]])]});
            var Q1;
            Q1=makeQuery(id+"F27.imprint","IMPRINT",FACE,{"disambiguationData":[TD([[makeQuery(id+"F27.imprint","IMPRINT",EDGE,{"derivedFrom":sQuery(id+"F27.wireOp",EDGE,"E59.0")}),-1.0]])]});
            extrude(context, id + "F28", {"entities" : qUnion([Q0, Q1]), "operationType" : NewBodyOperationType.ADD, "depth" : 20 * mm, "offsetDistance" : 25 * mm});
        }
        {
            var Q0;
            {var subQ0=sQuery(id+"F0.wireOp",EDGE,"E44.bottom");Q0=makeQuery(id+"F28.boolean.opBoolean","MERGE",FACE,{"derivedFrom":[makeQuery(id+"F26.opExtrude","SWEPT_FACE",FACE,{"disambiguationData":[OSD([subQ0])]}),makeQuery(id+"F28.opExtrude","SWEPT_FACE",FACE,{"disambiguationData":[OSD([subQ0])]})]});}
            var sketch = newSketch(context, id + "F29", { "sketchPlane" : qUnion([Q0])});
            skLineSegment(sketch, "E60.bottom", {"start": v(-43.5, 29.2) * mm, "end": v(70.5, 29.2) * mm});
            skLineSegment(sketch, "E60.top", {"start": v(-43.5, 32.2) * mm, "end": v(70.5, 32.2) * mm});
            skLineSegment(sketch, "E60.left", {"start": v(-43.5, 29.2) * mm, "end": v(-43.5, 32.2) * mm});
            skLineSegment(sketch, "E60.right", {"start": v(70.5, 29.2) * mm, "end": v(70.5, 32.2) * mm});
            skSolve(sketch);
        }
        {
            var Q0;
            Q0=makeQuery(id+"F29.imprint","IMPRINT",FACE,{"disambiguationData":[TD([[makeQuery(id+"F29.imprint","IMPRINT",EDGE,{"derivedFrom":sQuery(id+"F29.wireOp",EDGE,"E60.bottom")}),-1.0]])]});
            var Q1;
            {var subQ0=sQuery(id+"F0.wireOp",EDGE,"E44.top");Q1=makeQuery(id+"F28.boolean.opBoolean","MERGE",FACE,{"derivedFrom":[makeQuery(id+"F26.opExtrude","SWEPT_FACE",FACE,{"disambiguationData":[OSD([subQ0])]}),makeQuery(id+"F28.opExtrude","SWEPT_FACE",FACE,{"disambiguationData":[OSD([subQ0])]})]});}
            extrude(context, id + "F30", {"entities" : qUnion([Q0]), "operationType" : NewBodyOperationType.ADD, "endBound" : BoundingType.UP_TO_SURFACE, "oppositeDirection" : true, "depth" : 25 * mm, "endBoundEntityFace" : qUnion([Q1]), "offsetDistance" : 25 * mm});
        }
        {
            var Q0;
            {var subQ0=sQuery(id+"F0.wireOp",EDGE,"E44.top");var subQ1=sQuery(id+"F0.wireOp",EDGE,"E44.right");Q0=makeQuery(id+"F30.boolean.opBoolean","MERGE",EDGE,{"derivedFrom":[makeQuery(id+"F28.boolean.opBoolean","MERGE",EDGE,{"derivedFrom":[makeQuery(id+"F26.opExtrude","SWEPT_EDGE",EDGE,{"disambiguationData":[OSD([subQ0,subQ1])]}),makeQuery(id+"F28.opExtrude","SWEPT_EDGE",EDGE,{"disambiguationData":[OSD([subQ0,subQ1])]})]}),makeQuery(id+"F30.opExtrude","TWEAK_EDGE",EDGE,{"derivedFrom":[makeQuery(id+"F28.boolean.opBoolean","MERGE",FACE,{"derivedFrom":[makeQuery(id+"F26.opExtrude","SWEPT_FACE",FACE,{"disambiguationData":[OSD([subQ0])]}),makeQuery(id+"F28.opExtrude","SWEPT_FACE",FACE,{"disambiguationData":[OSD([subQ0])]})]}),makeQuery(id+"F29.imprint","IMPRINT",EDGE,{"derivedFrom":sQuery(id+"F29.wireOp",EDGE,"E60.left")})]})]});}
            var Q1;
            Q1=makeQuery(id+"F26.opExtrude","SWEPT_EDGE",EDGE,{"disambiguationData":[OSD([sQuery(id+"F22.wireOp",EDGE,"E58.2"),sQuery(id+"F22.wireOp",EDGE,"E58.3")])]});
            var Q2;
            Q2=makeQuery(id+"F28.opExtrude","SWEPT_EDGE",EDGE,{"disambiguationData":[OSD([sQuery(id+"F27.wireOp",EDGE,"E59.2"),sQuery(id+"F27.wireOp",EDGE,"E59.3")])]});
            var Q3;
            Q3=makeQuery(id+"F26.opExtrude","SWEPT_EDGE",EDGE,{"disambiguationData":[OSD([sQuery(id+"F22.wireOp",EDGE,"E58.1"),sQuery(id+"F22.wireOp",EDGE,"E58.2")])]});
            var Q4;
            Q4=makeQuery(id+"F28.opExtrude","SWEPT_EDGE",EDGE,{"disambiguationData":[OSD([sQuery(id+"F27.wireOp",EDGE,"E59.1"),sQuery(id+"F27.wireOp",EDGE,"E59.2")])]});
            var Q5;
            Q5=makeQuery(id+"F26.opExtrude","SWEPT_EDGE",EDGE,{"disambiguationData":[OSD([sQuery(id+"F22.wireOp",EDGE,"E58.0"),sQuery(id+"F22.wireOp",EDGE,"E58.1")])]});
            var Q6;
            Q6=makeQuery(id+"F28.opExtrude","SWEPT_EDGE",EDGE,{"disambiguationData":[OSD([sQuery(id+"F27.wireOp",EDGE,"E59.0"),sQuery(id+"F27.wireOp",EDGE,"E59.1")])]});
            var Q7;
            Q7=makeQuery(id+"F26.opExtrude","SWEPT_EDGE",EDGE,{"disambiguationData":[OSD([sQuery(id+"F22.wireOp",EDGE,"E58.0"),sQuery(id+"F22.wireOp",EDGE,"E58.3")])]});
            var Q8;
            {var subQ0=sQuery(id+"F0.wireOp",EDGE,"E44.top");var subQ1=sQuery(id+"F0.wireOp",EDGE,"E44.left");Q8=makeQuery(id+"F30.boolean.opBoolean","MERGE",EDGE,{"derivedFrom":[makeQuery(id+"F28.boolean.opBoolean","MERGE",EDGE,{"derivedFrom":[makeQuery(id+"F26.opExtrude","SWEPT_EDGE",EDGE,{"disambiguationData":[OSD([subQ0,subQ1])]}),makeQuery(id+"F28.opExtrude","SWEPT_EDGE",EDGE,{"disambiguationData":[OSD([subQ0,subQ1])]})]}),makeQuery(id+"F30.opExtrude","TWEAK_EDGE",EDGE,{"derivedFrom":[makeQuery(id+"F28.boolean.opBoolean","MERGE",FACE,{"derivedFrom":[makeQuery(id+"F26.opExtrude","SWEPT_FACE",FACE,{"disambiguationData":[OSD([subQ0])]}),makeQuery(id+"F28.opExtrude","SWEPT_FACE",FACE,{"disambiguationData":[OSD([subQ0])]})]}),makeQuery(id+"F29.imprint","IMPRINT",EDGE,{"derivedFrom":sQuery(id+"F29.wireOp",EDGE,"E60.right")})]})]});}
            var Q9;
            {var subQ0=sQuery(id+"F0.wireOp",EDGE,"E44.left");var subQ1=sQuery(id+"F0.wireOp",EDGE,"E44.bottom");Q9=makeQuery(id+"F30.boolean.opBoolean","MERGE",EDGE,{"derivedFrom":[makeQuery(id+"F28.boolean.opBoolean","MERGE",EDGE,{"derivedFrom":[makeQuery(id+"F26.opExtrude","SWEPT_EDGE",EDGE,{"disambiguationData":[OSD([subQ1,subQ0])]}),makeQuery(id+"F28.opExtrude","SWEPT_EDGE",EDGE,{"disambiguationData":[OSD([subQ1,subQ0])]})]}),makeQuery(id+"F30.opExtrude","CAP_EDGE",EDGE,{"disambiguationData":[OSD([sQuery(id+"F29.wireOp",EDGE,"E60.right")])],"isStart":true})]});}
            var Q10;
            {var subQ0=sQuery(id+"F0.wireOp",EDGE,"E44.right");var subQ1=sQuery(id+"F0.wireOp",EDGE,"E44.bottom");Q10=makeQuery(id+"F30.boolean.opBoolean","MERGE",EDGE,{"derivedFrom":[makeQuery(id+"F28.boolean.opBoolean","MERGE",EDGE,{"derivedFrom":[makeQuery(id+"F26.opExtrude","SWEPT_EDGE",EDGE,{"disambiguationData":[OSD([subQ1,subQ0])]}),makeQuery(id+"F28.opExtrude","SWEPT_EDGE",EDGE,{"disambiguationData":[OSD([subQ1,subQ0])]})]}),makeQuery(id+"F30.opExtrude","CAP_EDGE",EDGE,{"disambiguationData":[OSD([sQuery(id+"F29.wireOp",EDGE,"E60.left")])],"isStart":true})]});}
            fillet(context, id + "F31", {"entities" : qUnion([Q0, Q1, Q2, Q3, Q4, Q5, Q6, Q7, Q8, Q9, Q10]), "radius" : 5 * mm, "tangentPropagation" : true, "allowEdgeOverflow" : false});
        }
    });
